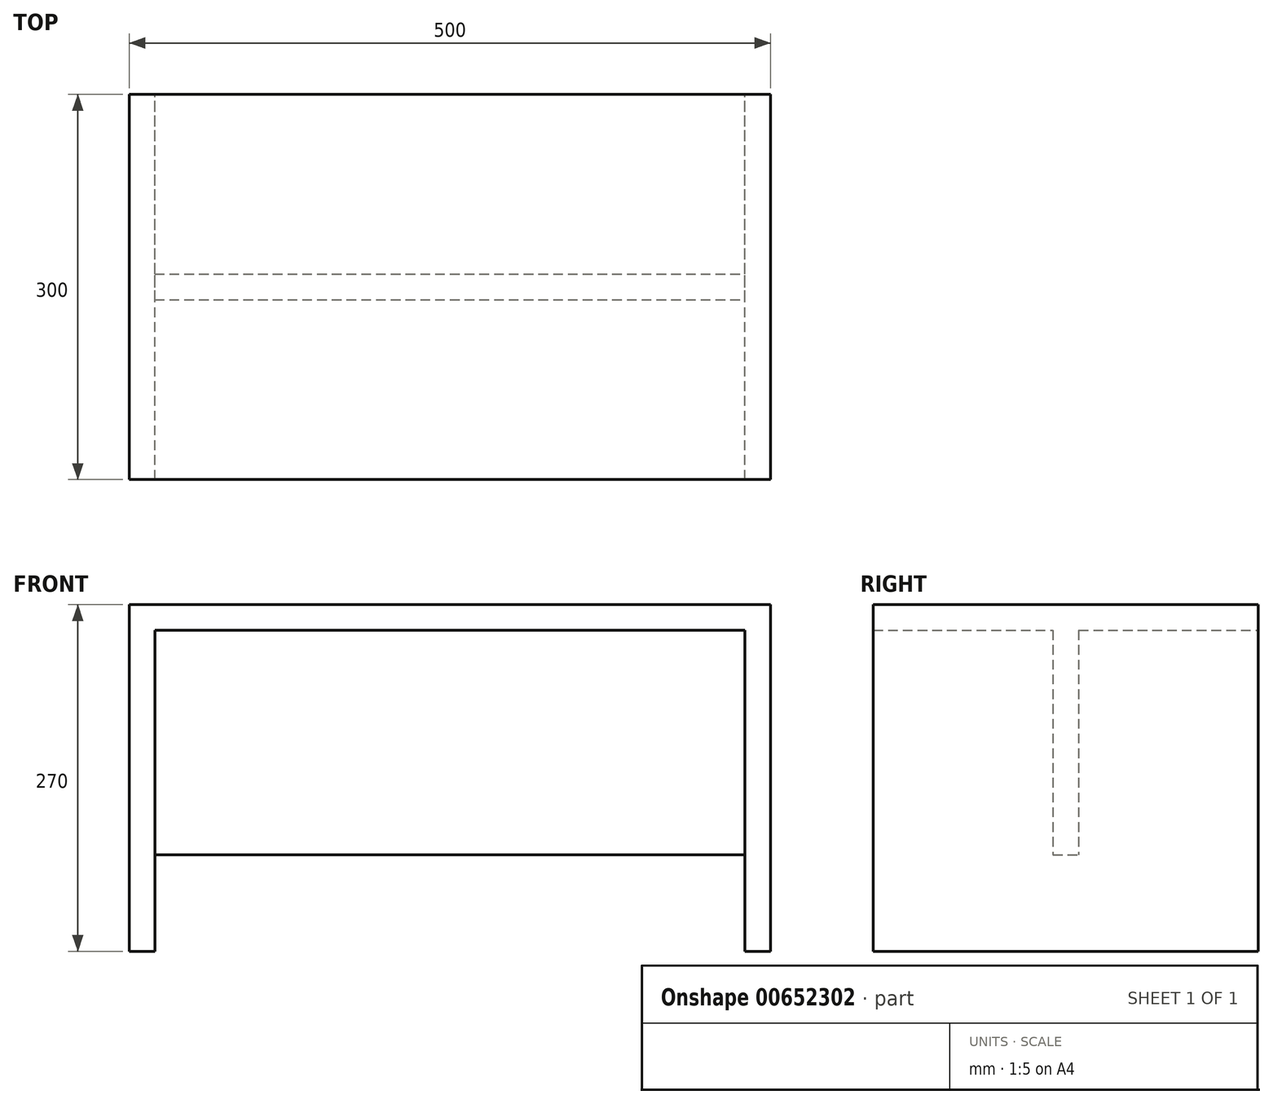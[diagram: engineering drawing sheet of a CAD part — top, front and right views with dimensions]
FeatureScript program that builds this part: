
annotation { "Feature Type Name" : "Feature", "Feature Type Description" : "" }
export const myFeature = defineFeature(function(context is Context, id is Id, definition is map)
    precondition{}
    {
        {
            var Q0;
            Q0=qCreatedBy(makeId("Front.planeOp"),FACE);
            var sketch = newSketch(context, id + "F0", { "sketchPlane" : qUnion([Q0])});
            skLineSegment(sketch, "E0.bottom", {"start": v(-250, 10) * mm, "end": v(250, 10) * mm});
            skLineSegment(sketch, "E0.top", {"start": v(-250, -10) * mm, "end": v(250, -10) * mm});
            skLineSegment(sketch, "E0.left", {"start": v(-250, 10) * mm, "end": v(-250, -10) * mm});
            skLineSegment(sketch, "E0.right", {"start": v(250, 10) * mm, "end": v(250, -10) * mm});
            skPoint(sketch, "E0.middle", {"position": v(0, 0) * mm});
            skSolve(sketch);
        }
        {
            var Q0;
            Q0=qCreatedBy(makeId("Front.planeOp"),FACE);
            var sketch = newSketch(context, id + "F1", { "sketchPlane" : qUnion([Q0])});
            skLineSegment(sketch, "E1.bottom", {"start": v(-250, -10) * mm, "end": v(-230, -10) * mm});
            skLineSegment(sketch, "E1.top", {"start": v(-250, -260) * mm, "end": v(-230, -260) * mm});
            skLineSegment(sketch, "E1.left", {"start": v(-250, -10) * mm, "end": v(-250, -260) * mm});
            skLineSegment(sketch, "E1.right", {"start": v(-230, -10) * mm, "end": v(-230, -260) * mm});
            skSolve(sketch);
        }
        {
            var Q0;
            Q0=qCreatedBy(makeId("Front.planeOp"),FACE);
            var sketch = newSketch(context, id + "F2", { "sketchPlane" : qUnion([Q0])});
            skLineSegment(sketch, "E2.bottom", {"start": v(250, -10) * mm, "end": v(230, -10) * mm});
            skLineSegment(sketch, "E2.top", {"start": v(250, -260) * mm, "end": v(230, -260) * mm});
            skLineSegment(sketch, "E2.left", {"start": v(250, -10) * mm, "end": v(250, -260) * mm});
            skLineSegment(sketch, "E2.right", {"start": v(230, -10) * mm, "end": v(230, -260) * mm});
            skSolve(sketch);
        }
        {
            var Q0;
            Q0=qCreatedBy(makeId("Front.planeOp"),FACE);
            var sketch = newSketch(context, id + "F3", { "sketchPlane" : qUnion([Q0])});
            skLineSegment(sketch, "E3.bottom", {"start": v(-230, -10) * mm, "end": v(230, -10) * mm});
            skLineSegment(sketch, "E3.top", {"start": v(-230, -185) * mm, "end": v(230, -185) * mm});
            skLineSegment(sketch, "E3.left", {"start": v(-230, -10) * mm, "end": v(-230, -185) * mm});
            skLineSegment(sketch, "E3.right", {"start": v(230, -10) * mm, "end": v(230, -185) * mm});
            skSolve(sketch);
        }
        {
            var Q0;
            Q0 = qSketchRegion(id + "F0", true);
            extrude(context, id + "F4", {"entities" : qUnion([Q0]), "depth" : 300 * mm, "offsetDistance" : 25 * mm, "symmetric" : true});
        }
        {
            var Q0;
            Q0=makeQuery(id+"F1.imprint","IMPRINT",FACE,{"disambiguationData":[TD([[makeQuery(id+"F1.imprint","IMPRINT",EDGE,{"derivedFrom":sQuery(id+"F1.wireOp",EDGE,"E1.bottom")}),-1.0]])]});
            extrude(context, id + "F5", {"entities" : qUnion([Q0]), "operationType" : NewBodyOperationType.ADD, "depth" : 300 * mm, "offsetDistance" : 25 * mm, "symmetric" : true});
        }
        {
            var Q0;
            Q0=makeQuery(id+"F2.imprint","IMPRINT",FACE,{"disambiguationData":[TD([[makeQuery(id+"F2.imprint","IMPRINT",EDGE,{"derivedFrom":sQuery(id+"F2.wireOp",EDGE,"E2.bottom")}),1.0]])]});
            extrude(context, id + "F6", {"entities" : qUnion([Q0]), "operationType" : NewBodyOperationType.ADD, "depth" : 300 * mm, "offsetDistance" : 25 * mm, "symmetric" : true});
        }
        {
            var Q0;
            Q0=makeQuery(id+"F3.imprint","IMPRINT",FACE,{"disambiguationData":[TD([[makeQuery(id+"F3.imprint","IMPRINT",EDGE,{"derivedFrom":sQuery(id+"F3.wireOp",EDGE,"E3.bottom")}),-1.0]])]});
            extrude(context, id + "F7", {"entities" : qUnion([Q0]), "operationType" : NewBodyOperationType.ADD, "depth" : 20 * mm, "offsetDistance" : 25 * mm, "symmetric" : true});
        }
    });
